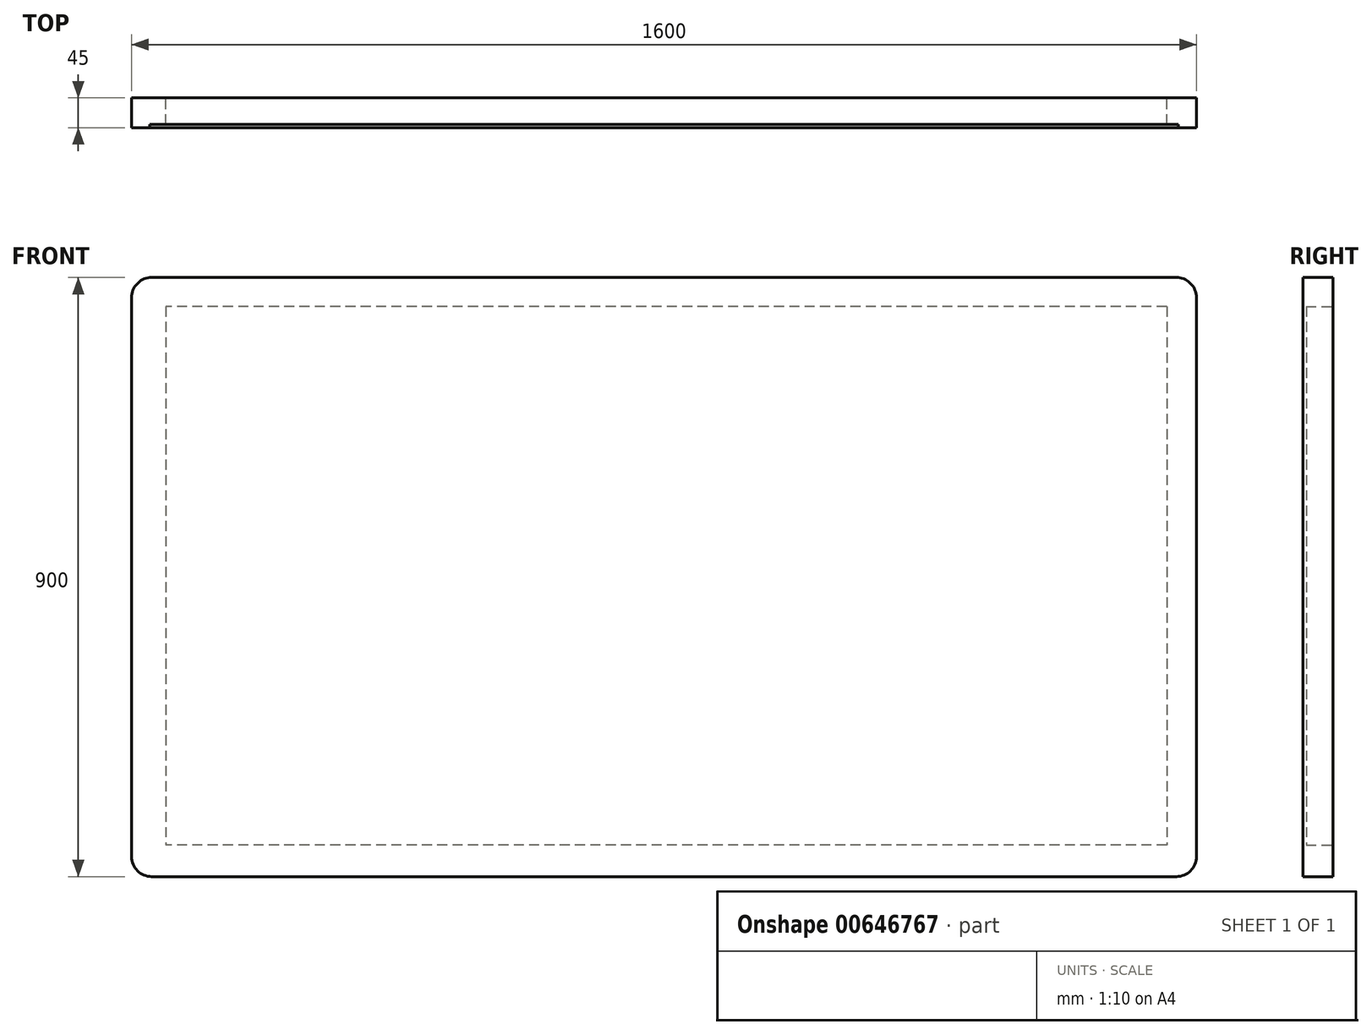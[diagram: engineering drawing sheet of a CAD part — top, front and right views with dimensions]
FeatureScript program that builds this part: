
annotation { "Feature Type Name" : "Feature", "Feature Type Description" : "" }
export const myFeature = defineFeature(function(context is Context, id is Id, definition is map)
    precondition{}
    {
        {
            var Q0;
            Q0=qCreatedBy(makeId("Front.planeOp"),FACE);
            var sketch = newSketch(context, id + "F0", { "sketchPlane" : qUnion([Q0])});
            skLineSegment(sketch, "E0.bottom", {"start": v(830.86, 480.82) * mm, "end": v(-769.14, 480.82) * mm});
            skLineSegment(sketch, "E0.top", {"start": v(830.86, -419.18) * mm, "end": v(-769.14, -419.18) * mm});
            skLineSegment(sketch, "E0.left", {"start": v(830.86, 480.82) * mm, "end": v(830.86, -419.18) * mm});
            skLineSegment(sketch, "E0.right", {"start": v(-769.14, 480.82) * mm, "end": v(-769.14, -419.18) * mm});
            skLineSegment(sketch, "E1.bottom", {"start": v(786.23, 437.03) * mm, "end": v(-718.04, 437.03) * mm});
            skLineSegment(sketch, "E1.top", {"start": v(786.23, -371.72) * mm, "end": v(-718.04, -371.72) * mm});
            skLineSegment(sketch, "E1.left", {"start": v(786.23, 437.03) * mm, "end": v(786.23, -371.72) * mm});
            skLineSegment(sketch, "E1.right", {"start": v(-718.04, 437.03) * mm, "end": v(-718.04, -371.72) * mm});
            skSolve(sketch);
        }
        {
            var Q0;
            Q0=makeQuery(id+"F0.imprint","IMPRINT",FACE,{"disambiguationData":[TD([[makeQuery(id+"F0.imprint","IMPRINT",EDGE,{"derivedFrom":sQuery(id+"F0.wireOp",EDGE,"E0.bottom")}),1.0]])]});
            extrude(context, id + "F1", {"entities" : qUnion([Q0]), "depth" : 40 * mm, "offsetDistance" : 25 * mm});
        }
        {
            var Q0;
            Q0=makeQuery(id+"F1.opExtrude","CAP_FACE",FACE,{"disambiguationData":[OSD([sQuery(id+"F0.wireOp",EDGE,"E0.bottom"),sQuery(id+"F0.wireOp",EDGE,"E0.top"),sQuery(id+"F0.wireOp",EDGE,"E0.left"),sQuery(id+"F0.wireOp",EDGE,"E0.right"),sQuery(id+"F0.wireOp",EDGE,"E1.bottom"),sQuery(id+"F0.wireOp",EDGE,"E1.top"),sQuery(id+"F0.wireOp",EDGE,"E1.left"),sQuery(id+"F0.wireOp",EDGE,"E1.right")])],"isStart":false});
            var sketch = newSketch(context, id + "F2", { "sketchPlane" : qUnion([Q0])});
            skLineSegment(sketch, "E2.bottom", {"start": v(830.86, -419.18) * mm, "end": v(-769.14, -419.18) * mm});
            skLineSegment(sketch, "E2.top", {"start": v(830.86, 480.71) * mm, "end": v(-769.14, 480.71) * mm});
            skLineSegment(sketch, "E2.left", {"start": v(830.86, -419.18) * mm, "end": v(830.86, 480.71) * mm});
            skLineSegment(sketch, "E2.right", {"start": v(-769.14, -419.18) * mm, "end": v(-769.14, 480.71) * mm});
            skSolve(sketch);
        }
        {
            var Q0;
            Q0 = qSketchRegion(id + "F2", true);
            extrude(context, id + "F3", {"entities" : qUnion([Q0]), "operationType" : NewBodyOperationType.ADD, "depth" : 5 * mm, "offsetDistance" : 25 * mm});
        }
        {
            var Q0;
            Q0=makeQuery(id+"F3.boolean.opBoolean","MERGE",EDGE,{"derivedFrom":[makeQuery(id+"F1.opExtrude","SWEPT_EDGE",EDGE,{"disambiguationData":[OSD([sQuery(id+"F0.wireOp",EDGE,"E0.top"),sQuery(id+"F0.wireOp",EDGE,"E0.left")])]}),makeQuery(id+"F3.opExtrude","SWEPT_EDGE",EDGE,{"disambiguationData":[OSD([sQuery(id+"F2.wireOp",EDGE,"E2.bottom"),sQuery(id+"F2.wireOp",EDGE,"E2.left")])]})]});
            var Q1;
            Q1=makeQuery(id+"F3.boolean.opBoolean","MERGE",EDGE,{"derivedFrom":[makeQuery(id+"F1.opExtrude","SWEPT_EDGE",EDGE,{"disambiguationData":[OSD([sQuery(id+"F0.wireOp",EDGE,"E0.top"),sQuery(id+"F0.wireOp",EDGE,"E0.right")])]}),makeQuery(id+"F3.opExtrude","SWEPT_EDGE",EDGE,{"disambiguationData":[OSD([sQuery(id+"F2.wireOp",EDGE,"E2.bottom"),sQuery(id+"F2.wireOp",EDGE,"E2.right")])]})]});
            var Q2;
            Q2=makeQuery(id+"F1.opExtrude","SWEPT_EDGE",EDGE,{"disambiguationData":[OSD([sQuery(id+"F0.wireOp",EDGE,"E0.bottom"),sQuery(id+"F0.wireOp",EDGE,"E0.right")])]});
            var Q3;
            Q3=makeQuery(id+"F1.opExtrude","SWEPT_EDGE",EDGE,{"disambiguationData":[OSD([sQuery(id+"F0.wireOp",EDGE,"E0.bottom"),sQuery(id+"F0.wireOp",EDGE,"E0.left")])]});
            fillet(context, id + "F4", {"entities" : qUnion([Q0, Q1, Q2, Q3]), "radius" : 30 * mm, "tangentPropagation" : true, "allowEdgeOverflow" : false});
        }
    });
